# Revit family: Basketball_Backstop-PSS-3305-Ceiling_Hung
name_source: partatom
category: Specialty Equipment
revit_build: Autodesk Revit 2017 (Build: 20170816_0615(x64)
units: mm (PartAtom-declared; Revit-internal decimal feet)

## family parameters
Always vertical = Yes
Cut with Voids When Loaded = No
OmniClass Number = 23.40.50.34.14.11
OmniClass Title = Backstops
Part Type = Normal
Room Calculation Point = No
Round Connector Dimension = Use Diameter
Shared = No
Work Plane-Based = No

## types (1)
- 24'-0" to 25'-11 7/8"
    Assembly Code = E1020900
    BIM Version = v3.1
    CSI MasterFormat = 11 66 23
    Description = Ceiling-Hung, Rear-Fold, Rear-Braced Roll-Fold Basketball Backstop
    Dim A Rear Brace = 7' - 11"
    Dim B Front Superstructure = 6' - 0"
    Dim C Mast Width = 6' - 9"
    Front Vertical Tube Length = 11"
    Installation Limitations = 18' to 30' Attachment A.F.F.
    Manufacturer = Performance Sports Systems
    Model = 3305
    Product Page URL = http://www.perfsports.com
    Superstructure Finish = Powder Coat - Performance Sports Systems - Black
    Sway Brace Height = 7' - 7 3/4"
    URL = http://www.perfsports.com

## geometry (parser evidence)
native form markers: Blend x23, Sweep x35
no freeform markers — native parametric forms only
